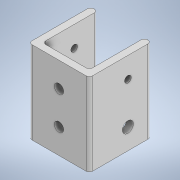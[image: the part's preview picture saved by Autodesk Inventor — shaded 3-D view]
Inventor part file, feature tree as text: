
AUTODESK INVENTOR PART (.ipt)
format: ipt  version: 2020 (Build 240168000, 168)  size: 161,280 bytes
history: native  units: in
note: dims shown in document units (in); Inventor stores cm internally (conversion verified against a paired STEP export)
features: extrude x3, sketch x3, fillet x1
ambient origin geometry x8: Origin, YZ Plane, XZ Plane, XY Plane, X Axis, Y Axis, Z Axis, Center Point
bodies: Solid1 (feature_tree)
feature tree (7):
  extrude  "Extrusion1"  Depth=1.0in
  sketch  "Sketch2"  dims[d2=0.125in d3=1.125in]
  sketch  "Sketch3"  dims[d4=0.125in d5=1.5in d6=0.0in d7=0.45in d8=90.0deg d9=0.45in d10=90.0deg d11=0.17in d12=0.17in d13=0.425in d14=0.375in d15=90.0deg d16=0.375in d17=90.0deg d18=0.12in d19=0.2in d20=1.5in d21=0.0in d22=1.5in d23=0.0in d24=0.06in]
  extrude  "Extrusion2"  Depth=1.125in
  extrude  "Extrusion3"  Depth=1.5in TaperAngle=0.0deg
  fillet  "Fillet1"  Radius=0.45in
  sketch  "Sketch1"  dims[d0=0.85in d1=1.0in]
